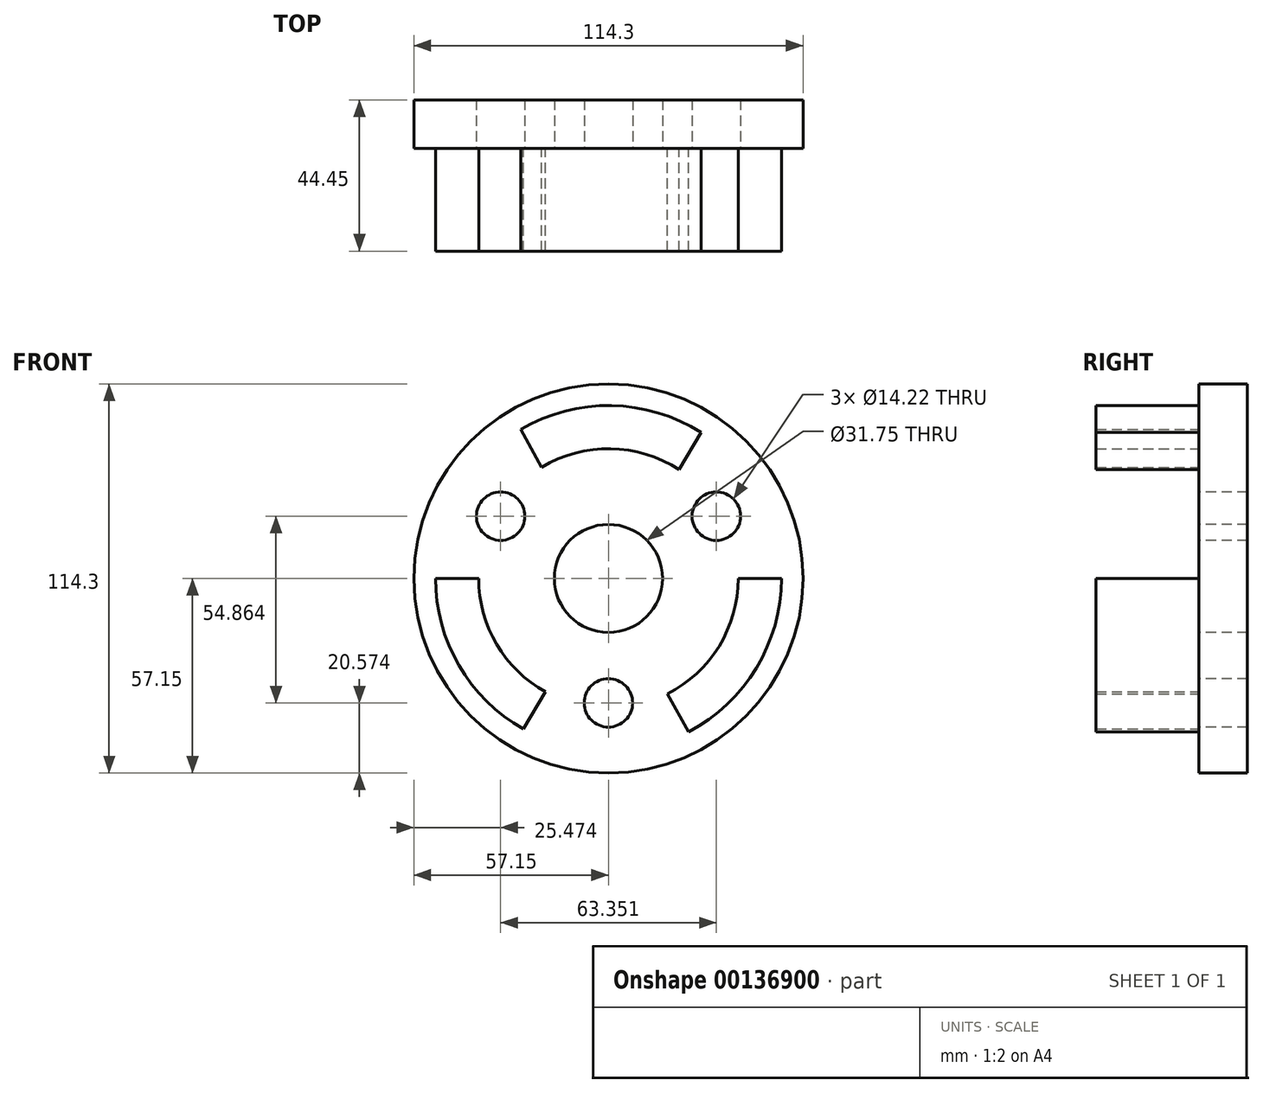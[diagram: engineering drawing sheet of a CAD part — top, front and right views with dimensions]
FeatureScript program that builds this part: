
annotation { "Feature Type Name" : "Feature", "Feature Type Description" : "" }
export const myFeature = defineFeature(function(context is Context, id is Id, definition is map)
    precondition{}
    {
        {
            var Q0;
            Q0=qCreatedBy(makeId("Front.planeOp"),FACE);
            var sketch = newSketch(context, id + "F0", { "sketchPlane" : qUnion([Q0])});
            skCircle(sketch, "E0", {"center": v(0, 0) * mm, "radius": 57.15 * mm});
            skSolve(sketch);
        }
        {
            var Q0;
            Q0 = qSketchRegion(id + "F0", true);
            extrude(context, id + "F1", {"entities" : qUnion([Q0]), "depth" : 14.22 * mm});
        }
        {
            var Q0;
            Q0=makeQuery(id+"F1.opExtrude","CAP_FACE",FACE,{"disambiguationData":[OSD([sQuery(id+"F0.wireOp",EDGE,"E0")])],"isStart":false});
            var sketch = newSketch(context, id + "F2", { "sketchPlane" : qUnion([Q0])});
            skCircle(sketch, "E1", {"center": v(0, 0) * mm, "radius": 15.88 * mm});
            skSolve(sketch);
        }
        {
            var Q0;
            Q0 = qSketchRegion(id + "F2", true);
            extrude(context, id + "F3", {"entities" : qUnion([Q0]), "operationType" : NewBodyOperationType.REMOVE, "endBound" : BoundingType.THROUGH_ALL, "oppositeDirection" : true, "depth" : 25.4 * mm});
        }
        {
            var Q0;
            Q0=makeQuery(id+"F1.opExtrude","CAP_FACE",FACE,{"disambiguationData":[OSD([sQuery(id+"F0.wireOp",EDGE,"E0")])],"isStart":false});
            var sketch = newSketch(context, id + "F4", { "sketchPlane" : qUnion([Q0])});
            skCircle(sketch, "E2", {"center": v(0, 0) * mm, "radius": 36.58 * mm, "construction": true});
            skCircle(sketch, "E3", {"center": v(0, -36.58) * mm, "radius": 7.11 * mm});
            skCircle(sketch, "E4.1.0", {"center": v(31.68, 18.29) * mm, "radius": 7.11 * mm});
            skCircle(sketch, "E4.2.0", {"center": v(-31.68, 18.29) * mm, "radius": 7.11 * mm});
            skSolve(sketch);
        }
        {
            var Q0;
            Q0 = qSketchRegion(id + "F4", true);
            extrude(context, id + "F5", {"entities" : qUnion([Q0]), "operationType" : NewBodyOperationType.REMOVE, "endBound" : BoundingType.THROUGH_ALL, "oppositeDirection" : true, "depth" : 25.4 * mm});
        }
        {
            var Q0;
            Q0=makeQuery(id+"F1.opExtrude","CAP_FACE",FACE,{"disambiguationData":[OSD([sQuery(id+"F0.wireOp",EDGE,"E0")])],"isStart":false});
            var sketch = newSketch(context, id + "F6", { "sketchPlane" : qUnion([Q0])});
            skCircle(sketch, "E5", {"center": v(-31.68, 18.29) * mm, "radius": 17.53 * mm, "construction": true});
            skCircle(sketch, "E6", {"center": v(31.68, 18.29) * mm, "radius": 17.53 * mm, "construction": true});
            skCircle(sketch, "E7", {"center": v(0, -36.58) * mm, "radius": 17.53 * mm, "construction": true});
            skArc(sketch, "E8", {"start": v(-38.1, 0) * mm, "mid": v(-32.83, -19.33) * mm, "end": v(-18.49, -33.32) * mm});
            skArc(sketch, "E9", {"start": v(-50.8, 0) * mm, "mid": v(-43.89, -25.59) * mm, "end": v(-25.03, -44.2) * mm});
            skLineSegment(sketch, "E10", {"start": v(-50.8, 0) * mm, "end": v(-38.1, 0) * mm});
            skLineSegment(sketch, "E11.trimOffspring", {"start": v(38.1, 0) * mm, "end": v(50.8, 0) * mm});
            skLineSegment(sketch, "E12", {"start": v(23.49, -45.04) * mm, "end": v(17.33, -33.93) * mm});
            skLineSegment(sketch, "E13", {"start": v(27.27, 42.86) * mm, "end": v(20.72, 31.97) * mm});
            skLineSegment(sketch, "E14.trimOffspring", {"start": v(-19.6, 32.67) * mm, "end": v(-25.77, 43.78) * mm});
            skLineSegment(sketch, "E15.trimOffspring", {"start": v(-18.49, -33.32) * mm, "end": v(-25.03, -44.2) * mm});
            skArc(sketch, "E16.trimOffspring", {"start": v(17.33, -33.93) * mm, "mid": v(32.5, -19.9) * mm, "end": v(38.1, 0) * mm});
            skArc(sketch, "E17.trimOffspring", {"start": v(23.49, -45.04) * mm, "mid": v(43.44, -26.34) * mm, "end": v(50.8, 0) * mm});
            skArc(sketch, "E18.trimOffspring", {"start": v(27.27, 42.86) * mm, "mid": v(0.88, 50.8) * mm, "end": v(-25.77, 43.78) * mm});
            skArc(sketch, "E19.trimOffspring", {"start": v(20.72, 31.97) * mm, "mid": v(0.66, 38.1) * mm, "end": v(-19.6, 32.67) * mm});
            skSolve(sketch);
        }
        {
            var Q0;
            Q0 = qSketchRegion(id + "F6", true);
            extrude(context, id + "F7", {"entities" : qUnion([Q0]), "operationType" : NewBodyOperationType.ADD, "depth" : 30.23 * mm});
        }
    });
